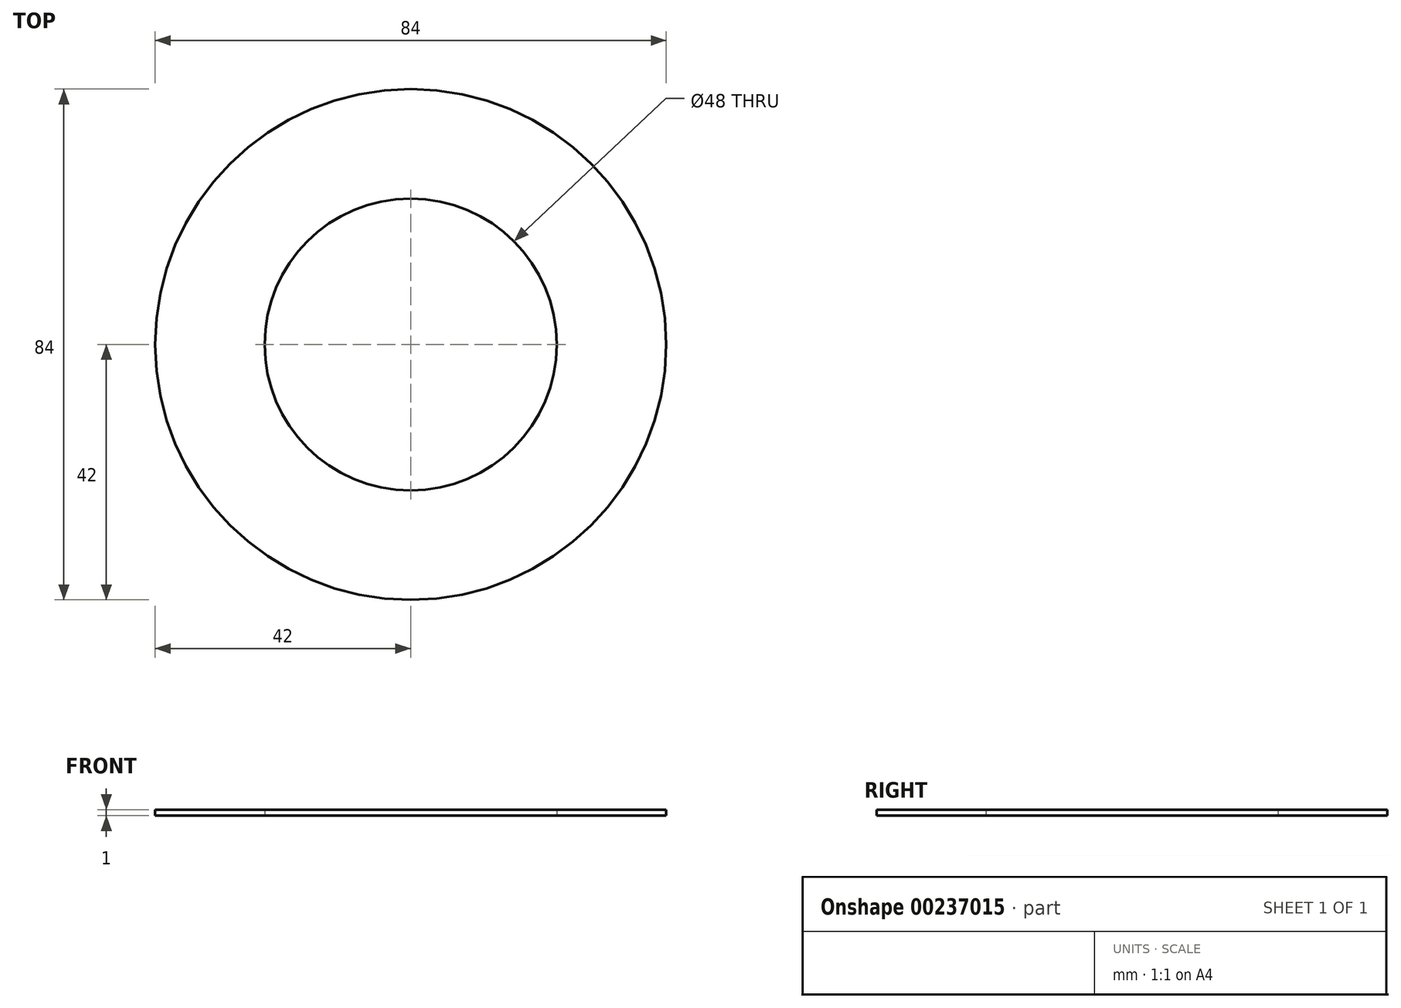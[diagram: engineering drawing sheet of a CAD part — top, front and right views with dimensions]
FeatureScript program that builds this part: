
annotation { "Feature Type Name" : "Feature", "Feature Type Description" : "" }
export const myFeature = defineFeature(function(context is Context, id is Id, definition is map)
    precondition{}
    {
        {
            var Q0;
            Q0=qCreatedBy(makeId("Front.planeOp"),FACE);
            var sketch = newSketch(context, id + "F0", { "sketchPlane" : qUnion([Q0])});
            skLineSegment(sketch, "E0", {"start": v(0, -0.85) * mm, "end": v(0, 41.83) * mm, "construction": true});
            skLineSegment(sketch, "E1.bottom", {"start": v(24, 0) * mm, "end": v(42, 0) * mm});
            skLineSegment(sketch, "E1.top", {"start": v(24, -1) * mm, "end": v(42, -1) * mm});
            skLineSegment(sketch, "E1.left", {"start": v(24, 0) * mm, "end": v(24, -1) * mm});
            skLineSegment(sketch, "E1.right", {"start": v(42, 0) * mm, "end": v(42, -1) * mm});
            skSolve(sketch);
        }
        {
            var Q0;
            Q0 = qSketchRegion(id + "F0", true);
            var Q1;
            Q1=sQuery(id+"F0.wireOp",EDGE,"E0");
            revolve(context, id + "F1", {"entities" : qUnion([Q0]), "axis" : qUnion([Q1]), "revolveType" : RevolveType.FULL});
        }
    });
